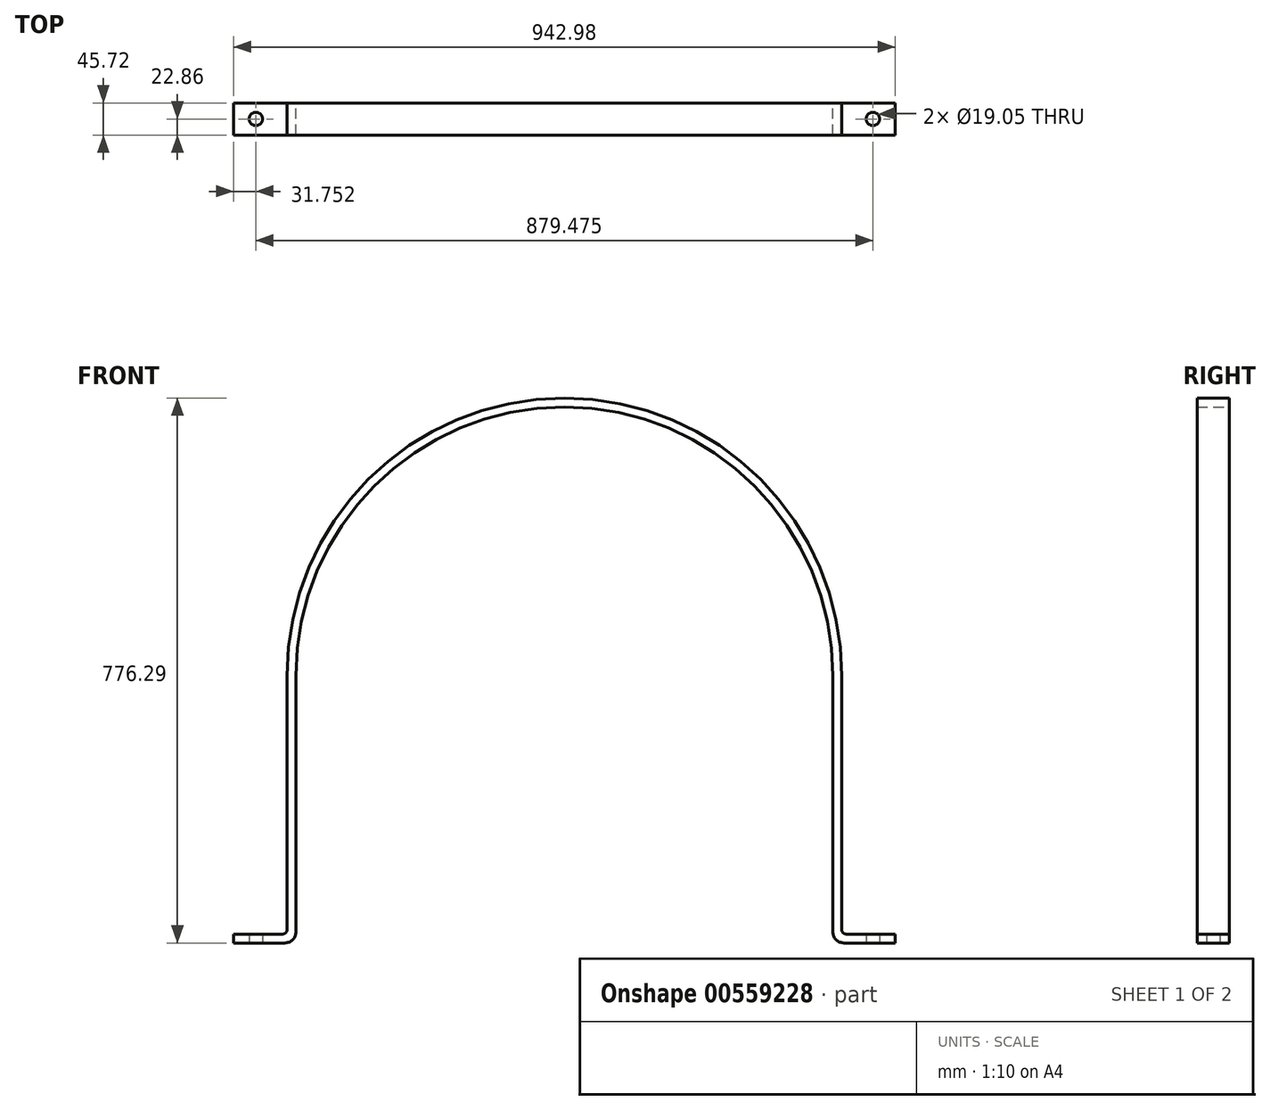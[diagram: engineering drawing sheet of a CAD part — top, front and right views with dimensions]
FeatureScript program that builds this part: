
annotation { "Feature Type Name" : "Feature", "Feature Type Description" : "" }
export const myFeature = defineFeature(function(context is Context, id is Id, definition is map)
    precondition{}
    {
        {
            var Q0;
            Q0=qCreatedBy(makeId("Front.planeOp"),FACE);
            var sketch = newSketch(context, id + "F0", { "sketchPlane" : qUnion([Q0])});
            skLineSegment(sketch, "E0.bottom", {"start": v(471.49, -381) * mm, "end": v(382.59, -381) * mm});
            skLineSegment(sketch, "E0.top", {"start": v(471.49, -368.3) * mm, "end": v(395.29, -368.3) * mm});
            skLineSegment(sketch, "E0.left", {"start": v(471.49, -381) * mm, "end": v(471.49, -368.3) * mm});
            skLineSegment(sketch, "E0.right", {"start": v(-471.49, -381) * mm, "end": v(-471.49, -368.3) * mm});
            skLineSegment(sketch, "E1", {"start": v(-382.59, 0) * mm, "end": v(-382.59, -381) * mm});
            skLineSegment(sketch, "E2", {"start": v(-395.29, 0) * mm, "end": v(-395.29, -368.3) * mm});
            skLineSegment(sketch, "E3", {"start": v(382.59, 0) * mm, "end": v(382.59, -381) * mm});
            skLineSegment(sketch, "E4", {"start": v(395.29, 0) * mm, "end": v(395.29, -368.3) * mm});
            skLineSegment(sketch, "E5.trimOffspring", {"start": v(-395.29, -368.3) * mm, "end": v(-471.49, -368.3) * mm});
            skLineSegment(sketch, "E6.trimOffspring", {"start": v(-382.59, -381) * mm, "end": v(-471.49, -381) * mm});
            skArc(sketch, "E7.trimOffspring", {"start": v(395.29, 0) * mm, "mid": v(0, 395.29) * mm, "end": v(-395.29, 0) * mm});
            skArc(sketch, "E8.trimOffspring", {"start": v(382.59, 0) * mm, "mid": v(0, 382.59) * mm, "end": v(-382.59, 0) * mm});
            skSolve(sketch);
        }
        {
            var Q0;
            Q0 = qSketchRegion(id + "F0", true);
            extrude(context, id + "F1", {"entities" : qUnion([Q0]), "endBound" : BoundingType.SYMMETRIC, "depth" : 45.72 * mm, "offsetDistance" : 25.4 * mm});
        }
        {
            var Q0;
            Q0=makeQuery(id+"F1.opExtrude","SWEPT_FACE",FACE,{"disambiguationData":[OSD([sQuery(id+"F0.wireOp",EDGE,"E6.trimOffspring")])]});
            var sketch = newSketch(context, id + "F2", { "sketchPlane" : qUnion([Q0])});
            skCircle(sketch, "E9", {"center": v(-439.74, 0) * mm, "radius": 9.53 * mm});
            skCircle(sketch, "E10.MirrorC", {"center": v(439.74, 0) * mm, "radius": 9.53 * mm});
            skSolve(sketch);
        }
        {
            var Q0;
            Q0 = qSketchRegion(id + "F2", true);
            extrude(context, id + "F3", {"entities" : qUnion([Q0]), "operationType" : NewBodyOperationType.REMOVE, "oppositeDirection" : true, "depth" : 25.4 * mm, "offsetDistance" : 25.4 * mm});
        }
        {
            var Q0;
            Q0=makeQuery(id+"F1.opExtrude","SWEPT_EDGE",EDGE,{"disambiguationData":[OSD([sQuery(id+"F0.wireOp",EDGE,"E2"),sQuery(id+"F0.wireOp",EDGE,"E5.trimOffspring")])]});
            var Q1;
            Q1=makeQuery(id+"F1.opExtrude","SWEPT_EDGE",EDGE,{"disambiguationData":[OSD([sQuery(id+"F0.wireOp",EDGE,"E0.top"),sQuery(id+"F0.wireOp",EDGE,"E4")])]});
            fillet(context, id + "F4", {"entities" : qUnion([Q0, Q1]), "radius" : 6.35 * mm, "tangentPropagation" : true, "allowEdgeOverflow" : false});
        }
        {
            var Q0;
            Q0=makeQuery(id+"F1.opExtrude","SWEPT_EDGE",EDGE,{"disambiguationData":[OSD([sQuery(id+"F0.wireOp",EDGE,"E1"),sQuery(id+"F0.wireOp",EDGE,"E6.trimOffspring")])]});
            var Q1;
            Q1=makeQuery(id+"F1.opExtrude","SWEPT_EDGE",EDGE,{"disambiguationData":[OSD([sQuery(id+"F0.wireOp",EDGE,"E0.bottom"),sQuery(id+"F0.wireOp",EDGE,"E3")])]});
            fillet(context, id + "F5", {"entities" : qUnion([Q0, Q1]), "radius" : 15.88 * mm, "tangentPropagation" : true, "allowEdgeOverflow" : false});
        }
    });
